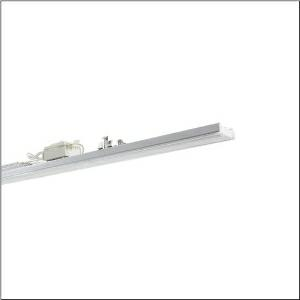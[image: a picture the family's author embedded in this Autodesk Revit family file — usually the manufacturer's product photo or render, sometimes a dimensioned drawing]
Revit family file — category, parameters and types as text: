
# Revit family: licross_11_recessed_ho_51tl11dv4m2s
name_source: partatom
category: Lighting Fixtures
units: mm (PartAtom-declared; Revit-internal decimal feet)

## family parameters
Cut with Voids When Loaded = No
Host = Face
Light Source = No
Part Type = Normal
Room Calculation Point = No
Round Connector Dimension = Use Diameter
Shared = No

## types (1)
- --- (1 x LED, 27080 lm, 150.5 W, 4000K)
    Apparent Load = 150 VA
    CIE Flux Codes = 87 95 99 100 100
    Color Rendering = 80
    Color Temperature = 4000K
    Default Elevation = 1800 mm
    Description = Licross 11 Recessed HO, luminaire insert, of sheet steel, coil coated, white, length: 2.250mm, width: 66mm, height: 67mm, LED rated luminous flux: 27.080lm, light colour: 840, SDCM (Standard Deviation of Colour Matching)MacAdam ≤ 2 SDCM (initial), control gear: DALI 2, with plug, 5-pole, with phase selection, mains connection: 220..240V, AC, 50/60Hz, rated input power: 151W, internal wiring halogen-free, primary light control with lens, of plastic, primary optical cover: cover, of PMMA, light emission: direct distribution, primary light characteristic: symmetric, protection rating (complete): IP40, insulation class (complete): insulation class I (protective earthing), certification: CE, ENEC, VDE, UKCA, protection symbol: D if used in an environment without relevant dust loads with corresponding accessories, impact resistance: IK06, permissible ambient temperature for indoor applications: -40..+35°C, corresponds to IFS (International Featured Standards) requirements for safety and quality in the food industry, reducing of maximum allowable ambient temperature of 5°C with ceiling mounting, LABS conformity tested according to VDMA 24364:2018-05, The light source and the operating device comply with the requirements of the Ecodesign Regulation (EU) 2019/2020 and are replaceable in accordance with this regulation, packaging unit: 1 piece
    Height = 58 mm
    Lamp = 1 x LED
    Lamp Light Flux = 27080 lm
    Lamp Power = 150.5 W
    Lamp count = 1
    Length = 2250 mm
    Luminous efficacy = 180 lm/W
    Manufacturer = Siteco
    ModVariant = No
    Model = 51TL11DV4M2S
    Mounting Place = Ceiling
    Mounting Type = Pendant
    Number of Poles = 1
    OnlyDefault = Yes
    Power Factor = 1
    Product Name = Licross 11 Recessed HO
    Product group = luminaire insert | ceiling pendant
    ProductGroupID = 901
    Protection Class = Protection class I
    Protection Degree = IP 40
    RLX_Detail_Level = 1
    RLX_Emergency_Light_Flux = 0 lm
    RLX_Emergency_Type = 0
    RLX_Emergency_Type_DB = No
    RlxData = <blob elided: 30001 chars, md5=983c3429>
    Socket = socket
    Standby Power = 0 W
    System Light Flux = 27079 lm
    System Power = 150 W
    Type Comments = factory setting: luminous flux: 100 % | dim-lin: 254 | 690 mA
    Type Image = l_1296930.jpg
    URL = http://relux.com
    VarID = @adj_100403
    Voltage = 0 V
    Weight = 0.00 kg
    Width = 66 mm

## geometry (parser evidence)
native form markers: Blend x4, Sweep x11
no freeform markers — native parametric forms only
